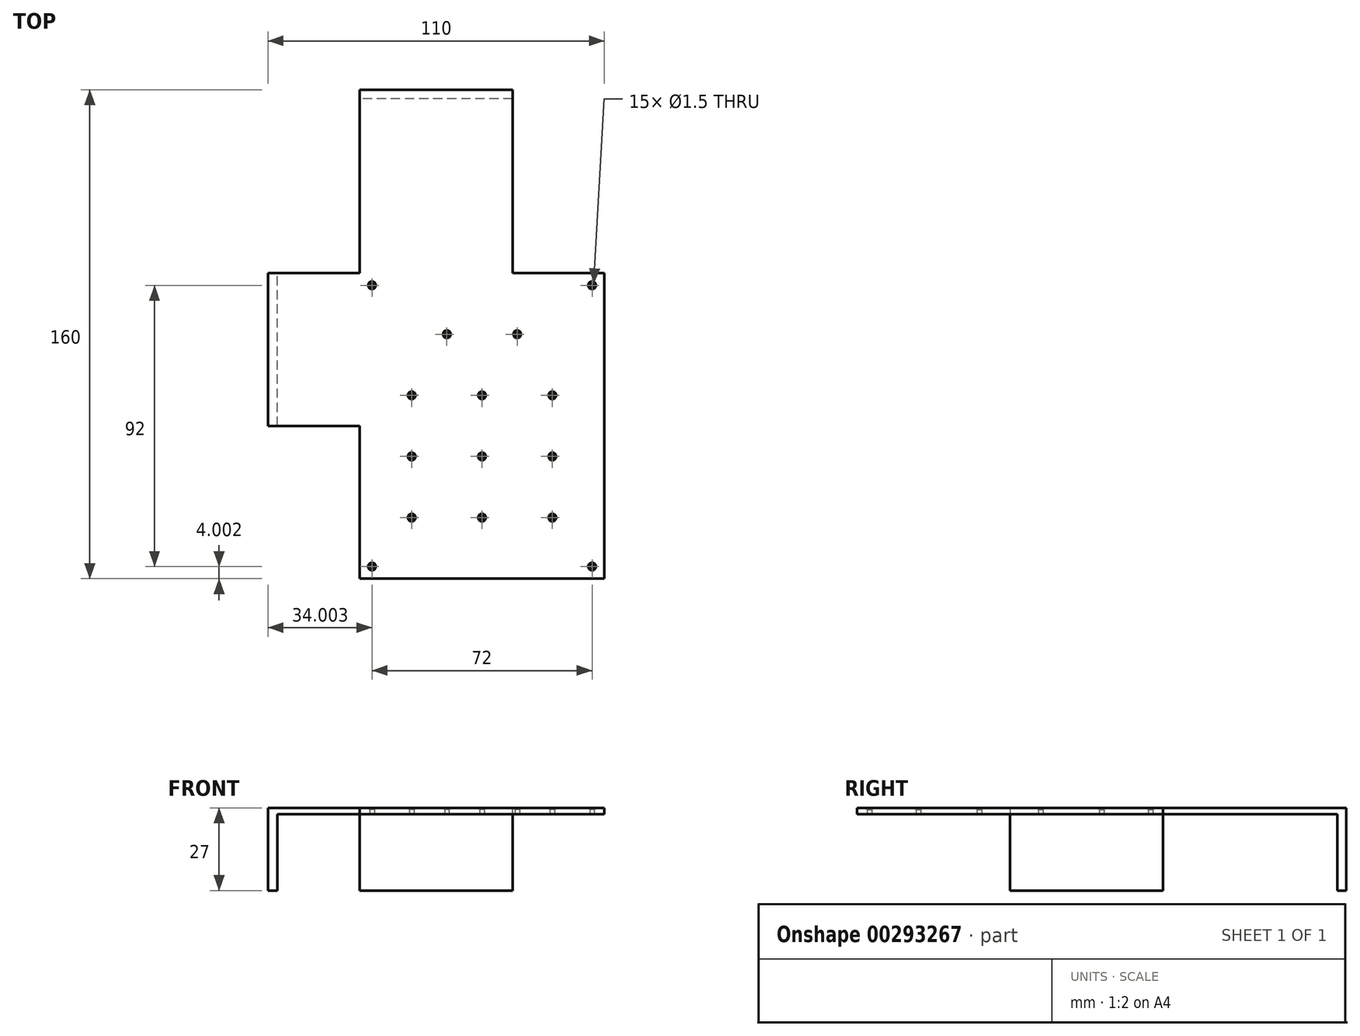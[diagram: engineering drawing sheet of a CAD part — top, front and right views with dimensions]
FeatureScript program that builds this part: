
annotation { "Feature Type Name" : "Feature", "Feature Type Description" : "" }
export const myFeature = defineFeature(function(context is Context, id is Id, definition is map)
    precondition{}
    {
        {
            var Q0;
            Q0=qCreatedBy(makeId("Top.planeOp"),FACE);
            var sketch = newSketch(context, id + "F0", { "sketchPlane" : qUnion([Q0])});
            skLineSegment(sketch, "E0.bottom", {"start": v(-60.4, 19.44) * mm, "end": v(19.6, 19.44) * mm});
            skLineSegment(sketch, "E0.top", {"start": v(-60.4, -80.56) * mm, "end": v(19.6, -80.56) * mm});
            skLineSegment(sketch, "E0.left", {"start": v(-60.4, 19.44) * mm, "end": v(-60.4, -80.56) * mm});
            skLineSegment(sketch, "E0.right", {"start": v(19.6, 19.44) * mm, "end": v(19.6, -80.56) * mm});
            skCircle(sketch, "E1", {"center": v(-43.4, -60.56) * mm, "radius": 0.75 * mm});
            skCircle(sketch, "E2.0.1.0", {"center": v(-43.4, -40.56) * mm, "radius": 0.75 * mm});
            skCircle(sketch, "E2.0.2.0", {"center": v(-43.4, -20.56) * mm, "radius": 0.75 * mm});
            skCircle(sketch, "E2.1.0.0", {"center": v(-20.4, -60.56) * mm, "radius": 0.75 * mm});
            skCircle(sketch, "E2.1.1.0", {"center": v(-20.4, -40.56) * mm, "radius": 0.75 * mm});
            skCircle(sketch, "E2.1.2.0", {"center": v(-20.4, -20.56) * mm, "radius": 0.75 * mm});
            skCircle(sketch, "E2.2.0.0", {"center": v(2.6, -60.56) * mm, "radius": 0.75 * mm});
            skCircle(sketch, "E2.2.1.0", {"center": v(2.6, -40.56) * mm, "radius": 0.75 * mm});
            skCircle(sketch, "E2.2.2.0", {"center": v(2.6, -20.56) * mm, "radius": 0.75 * mm});
            skLineSegment(sketch, "E2.direction1", {"start": v(-43.4, -60.56) * mm, "end": v(-20.4, -60.56) * mm, "construction": true});
            skLineSegment(sketch, "E2.direction2", {"start": v(-43.4, -60.56) * mm, "end": v(-43.4, -40.56) * mm, "construction": true});
            skCircle(sketch, "E3", {"center": v(-31.9, -0.56) * mm, "radius": 0.75 * mm});
            skCircle(sketch, "E4.1.0.0", {"center": v(-8.9, -0.56) * mm, "radius": 0.75 * mm});
            skLineSegment(sketch, "E4.direction1", {"start": v(-31.9, -0.56) * mm, "end": v(-8.9, -0.56) * mm, "construction": true});
            skCircle(sketch, "E5", {"center": v(-56.4, -76.56) * mm, "radius": 0.75 * mm});
            skCircle(sketch, "E6.0.1.0", {"center": v(-56.4, 15.44) * mm, "radius": 0.75 * mm});
            skCircle(sketch, "E6.1.0.0", {"center": v(15.6, -76.56) * mm, "radius": 0.75 * mm});
            skCircle(sketch, "E6.1.1.0", {"center": v(15.6, 15.44) * mm, "radius": 0.75 * mm});
            skLineSegment(sketch, "E6.direction1", {"start": v(-56.4, -76.56) * mm, "end": v(15.6, -76.56) * mm, "construction": true});
            skLineSegment(sketch, "E6.direction2", {"start": v(-56.4, -76.56) * mm, "end": v(-56.4, 15.44) * mm, "construction": true});
            skSolve(sketch);
        }
        {
            var Q0;
            Q0=makeQuery(id+"F0.imprint","IMPRINT",FACE,{"disambiguationData":[TD([[makeQuery(id+"F0.imprint","IMPRINT",EDGE,{"derivedFrom":sQuery(id+"F0.wireOp",EDGE,"E0.bottom")}),-1.0]])]});
            extrude(context, id + "F1", {"entities" : qUnion([Q0]), "depth" : 2 * mm});
        }
        {
            var Q0;
            Q0=makeQuery(id+"F1.opExtrude","SWEPT_FACE",FACE,{"disambiguationData":[OSD([sQuery(id+"F0.wireOp",EDGE,"E0.left")])]});
            var sketch = newSketch(context, id + "F2", { "sketchPlane" : qUnion([Q0])});
            skLineSegment(sketch, "E7.bottom", {"start": v(-19.44, 2) * mm, "end": v(30.56, 2) * mm});
            skLineSegment(sketch, "E7.top", {"start": v(-19.44, 0) * mm, "end": v(30.56, 0) * mm});
            skLineSegment(sketch, "E7.left", {"start": v(-19.44, 2) * mm, "end": v(-19.44, 0) * mm});
            skLineSegment(sketch, "E7.right", {"start": v(30.56, 2) * mm, "end": v(30.56, 0) * mm});
            skSolve(sketch);
        }
        {
            var Q0;
            Q0=makeQuery(id+"F1.opExtrude","SWEPT_FACE",FACE,{"disambiguationData":[OSD([sQuery(id+"F0.wireOp",EDGE,"E0.bottom")])]});
            var sketch = newSketch(context, id + "F3", { "sketchPlane" : qUnion([Q0])});
            skLineSegment(sketch, "E8.bottom", {"start": v(60.4, 0) * mm, "end": v(10.4, 0) * mm});
            skLineSegment(sketch, "E8.top", {"start": v(60.4, 2) * mm, "end": v(10.4, 2) * mm});
            skLineSegment(sketch, "E8.left", {"start": v(60.4, 0) * mm, "end": v(60.4, 2) * mm});
            skLineSegment(sketch, "E8.right", {"start": v(10.4, 0) * mm, "end": v(10.4, 2) * mm});
            skSolve(sketch);
        }
        {
            var Q0;
            Q0=makeQuery(id+"F3.imprint","IMPRINT",FACE,{"disambiguationData":[TD([[makeQuery(id+"F3.imprint","IMPRINT",EDGE,{"derivedFrom":sQuery(id+"F3.wireOp",EDGE,"E8.bottom")}),-1.0]])]});
            extrude(context, id + "F4", {"entities" : qUnion([Q0]), "operationType" : NewBodyOperationType.ADD, "depth" : 60 * mm});
        }
        {
            var Q0;
            Q0=makeQuery(id+"F2.imprint","IMPRINT",FACE,{"disambiguationData":[TD([[makeQuery(id+"F2.imprint","IMPRINT",EDGE,{"derivedFrom":sQuery(id+"F2.wireOp",EDGE,"E7.bottom")}),-1.0]])]});
            extrude(context, id + "F5", {"entities" : qUnion([Q0]), "operationType" : NewBodyOperationType.ADD, "depth" : 30 * mm});
        }
        {
            var Q0;
            Q0=makeQuery(id+"F5.boolean.opBoolean","MERGE",FACE,{"derivedFrom":[makeQuery(id+"F4.boolean.opBoolean","MERGE",FACE,{"derivedFrom":[makeQuery(id+"F1.opExtrude","CAP_FACE",FACE,{"disambiguationData":[OSD([sQuery(id+"F0.wireOp",EDGE,"E0.bottom"),sQuery(id+"F0.wireOp",EDGE,"E0.top"),sQuery(id+"F0.wireOp",EDGE,"E0.left"),sQuery(id+"F0.wireOp",EDGE,"E0.right"),sQuery(id+"F0.wireOp",EDGE,"E1"),sQuery(id+"F0.wireOp",EDGE,"E2.0.1.0"),sQuery(id+"F0.wireOp",EDGE,"E2.0.2.0"),sQuery(id+"F0.wireOp",EDGE,"E2.1.0.0"),sQuery(id+"F0.wireOp",EDGE,"E2.1.1.0"),sQuery(id+"F0.wireOp",EDGE,"E2.1.2.0"),sQuery(id+"F0.wireOp",EDGE,"E2.2.0.0"),sQuery(id+"F0.wireOp",EDGE,"E2.2.1.0"),sQuery(id+"F0.wireOp",EDGE,"E2.2.2.0"),sQuery(id+"F0.wireOp",EDGE,"E3"),sQuery(id+"F0.wireOp",EDGE,"E4.1.0.0"),sQuery(id+"F0.wireOp",EDGE,"E5"),sQuery(id+"F0.wireOp",EDGE,"E6.0.1.0"),sQuery(id+"F0.wireOp",EDGE,"E6.1.0.0"),sQuery(id+"F0.wireOp",EDGE,"E6.1.1.0")])],"isStart":true}),makeQuery(id+"F4.opExtrude","SWEPT_FACE",FACE,{"disambiguationData":[OSD([sQuery(id+"F3.wireOp",EDGE,"E8.bottom")])]})]}),makeQuery(id+"F5.opExtrude","SWEPT_FACE",FACE,{"disambiguationData":[OSD([sQuery(id+"F2.wireOp",EDGE,"E7.top")])]})]});
            var sketch = newSketch(context, id + "F6", { "sketchPlane" : qUnion([Q0])});
            skLineSegment(sketch, "E9.bottom", {"start": v(-90.4, 30.56) * mm, "end": v(-87.4, 30.56) * mm});
            skLineSegment(sketch, "E9.top", {"start": v(-90.4, -19.44) * mm, "end": v(-87.4, -19.44) * mm});
            skLineSegment(sketch, "E9.left", {"start": v(-90.4, 30.56) * mm, "end": v(-90.4, -19.44) * mm});
            skLineSegment(sketch, "E9.right", {"start": v(-87.4, 30.56) * mm, "end": v(-87.4, -19.44) * mm});
            skLineSegment(sketch, "E10.bottom", {"start": v(-10.4, -79.44) * mm, "end": v(-60.4, -79.44) * mm});
            skLineSegment(sketch, "E10.top", {"start": v(-10.4, -76.44) * mm, "end": v(-60.4, -76.44) * mm});
            skLineSegment(sketch, "E10.left", {"start": v(-10.4, -79.44) * mm, "end": v(-10.4, -76.44) * mm});
            skLineSegment(sketch, "E10.right", {"start": v(-60.4, -79.44) * mm, "end": v(-60.4, -76.44) * mm});
            skSolve(sketch);
        }
        {
            var Q0;
            Q0 = qSketchRegion(id + "F6", true);
            extrude(context, id + "F7", {"entities" : qUnion([Q0]), "operationType" : NewBodyOperationType.ADD, "depth" : 25 * mm});
        }
        {
            var Q0;
            Q0=makeQuery(id+"F1.opExtrude","CAP_EDGE",EDGE,{"disambiguationData":[OSD([sQuery(id+"F0.wireOp",EDGE,"E5")])],"isStart":false});
            var Q1;
            Q1=makeQuery(id+"F1.opExtrude","CAP_EDGE",EDGE,{"disambiguationData":[OSD([sQuery(id+"F0.wireOp",EDGE,"E1")])],"isStart":false});
            var Q2;
            Q2=makeQuery(id+"F1.opExtrude","CAP_EDGE",EDGE,{"disambiguationData":[OSD([sQuery(id+"F0.wireOp",EDGE,"E2.0.1.0")])],"isStart":false});
            var Q3;
            Q3=makeQuery(id+"F1.opExtrude","CAP_EDGE",EDGE,{"disambiguationData":[OSD([sQuery(id+"F0.wireOp",EDGE,"E2.0.2.0")])],"isStart":false});
            var Q4;
            Q4=makeQuery(id+"F1.opExtrude","CAP_EDGE",EDGE,{"disambiguationData":[OSD([sQuery(id+"F0.wireOp",EDGE,"E3")])],"isStart":false});
            var Q5;
            Q5=makeQuery(id+"F1.opExtrude","CAP_EDGE",EDGE,{"disambiguationData":[OSD([sQuery(id+"F0.wireOp",EDGE,"E2.1.2.0")])],"isStart":false});
            var Q6;
            Q6=makeQuery(id+"F1.opExtrude","CAP_EDGE",EDGE,{"disambiguationData":[OSD([sQuery(id+"F0.wireOp",EDGE,"E2.1.1.0")])],"isStart":false});
            var Q7;
            Q7=makeQuery(id+"F1.opExtrude","CAP_EDGE",EDGE,{"disambiguationData":[OSD([sQuery(id+"F0.wireOp",EDGE,"E2.1.0.0")])],"isStart":false});
            var Q8;
            Q8=makeQuery(id+"F1.opExtrude","CAP_EDGE",EDGE,{"disambiguationData":[OSD([sQuery(id+"F0.wireOp",EDGE,"E6.1.0.0")])],"isStart":false});
            var Q9;
            Q9=makeQuery(id+"F1.opExtrude","CAP_EDGE",EDGE,{"disambiguationData":[OSD([sQuery(id+"F0.wireOp",EDGE,"E2.2.0.0")])],"isStart":false});
            var Q10;
            Q10=makeQuery(id+"F1.opExtrude","CAP_EDGE",EDGE,{"disambiguationData":[OSD([sQuery(id+"F0.wireOp",EDGE,"E2.2.1.0")])],"isStart":false});
            var Q11;
            Q11=makeQuery(id+"F1.opExtrude","CAP_EDGE",EDGE,{"disambiguationData":[OSD([sQuery(id+"F0.wireOp",EDGE,"E2.2.2.0")])],"isStart":false});
            var Q12;
            Q12=makeQuery(id+"F1.opExtrude","CAP_EDGE",EDGE,{"disambiguationData":[OSD([sQuery(id+"F0.wireOp",EDGE,"E4.1.0.0")])],"isStart":false});
            var Q13;
            Q13=makeQuery(id+"F1.opExtrude","CAP_EDGE",EDGE,{"disambiguationData":[OSD([sQuery(id+"F0.wireOp",EDGE,"E6.1.1.0")])],"isStart":false});
            var Q14;
            Q14=makeQuery(id+"F1.opExtrude","CAP_EDGE",EDGE,{"disambiguationData":[OSD([sQuery(id+"F0.wireOp",EDGE,"E6.0.1.0")])],"isStart":false});
            chamfer(context, id + "F8", {"entities" : qUnion([Q0, Q1, Q2, Q3, Q4, Q5, Q6, Q7, Q8, Q9, Q10, Q11, Q12, Q13, Q14]), "width" : 0.5 * mm, "tangentPropagation" : true});
        }
    });
